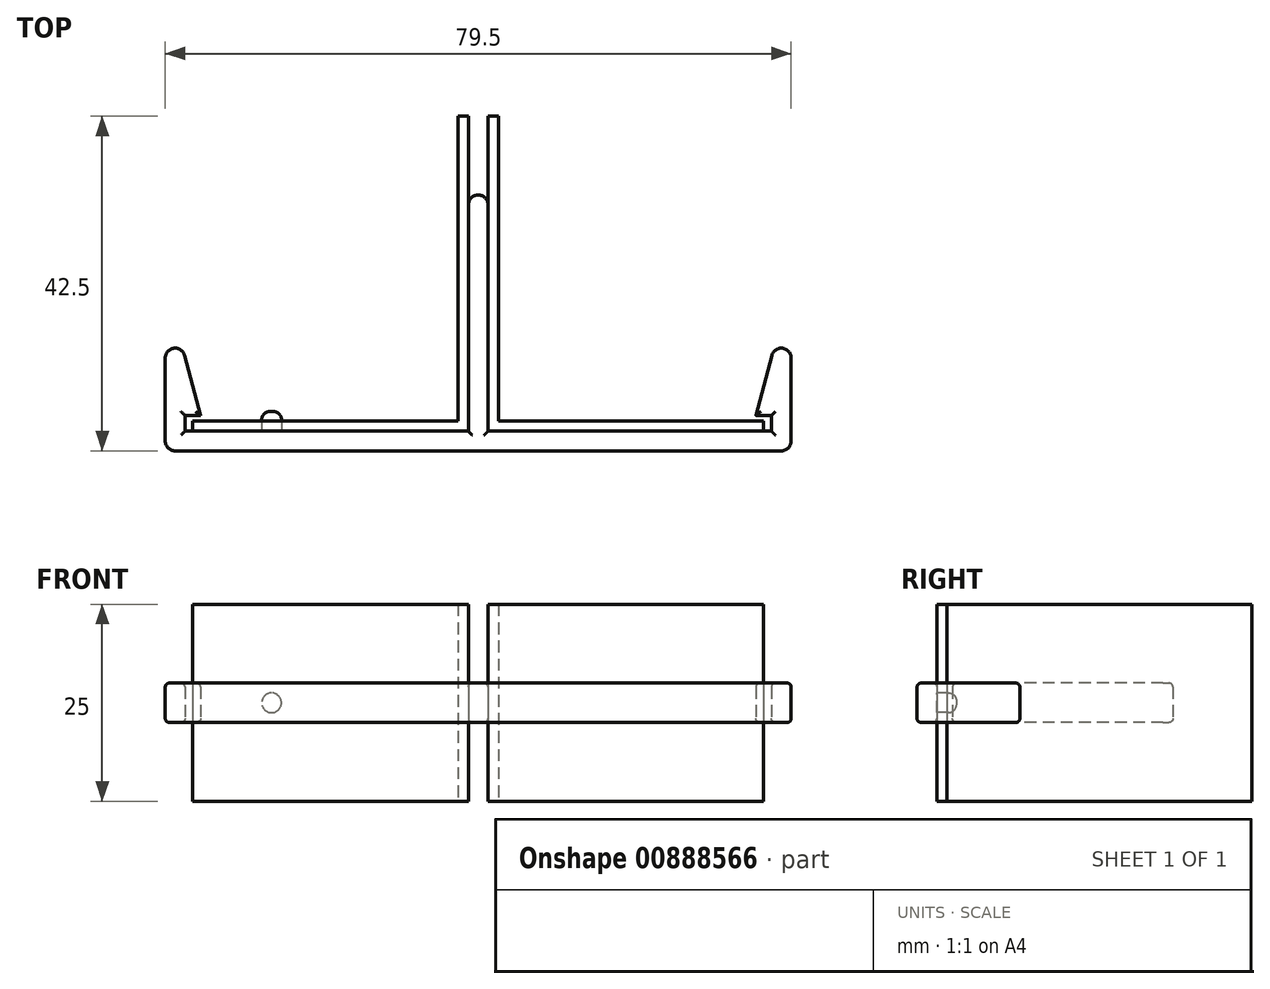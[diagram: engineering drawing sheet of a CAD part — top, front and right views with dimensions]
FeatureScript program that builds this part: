
annotation { "Feature Type Name" : "Feature", "Feature Type Description" : "" }
export const myFeature = defineFeature(function(context is Context, id is Id, definition is map)
    precondition{}
    {
        {
            var Q0;
            Q0=qCreatedBy(makeId("Top.planeOp"),FACE);
            var sketch = newSketch(context, id + "F0", { "sketchPlane" : qUnion([Q0])});
            skLineSegment(sketch, "E0", {"start": v(-1.25, 0) * mm, "end": v(-1.25, 40) * mm});
            skLineSegment(sketch, "E1", {"start": v(-1.25, 40) * mm, "end": v(-2.55, 40) * mm});
            skLineSegment(sketch, "E2", {"start": v(-2.55, 40) * mm, "end": v(-2.55, 1.3) * mm});
            skLineSegment(sketch, "E3", {"start": v(-2.55, 1.3) * mm, "end": v(-36.25, 1.3) * mm});
            skLineSegment(sketch, "E4", {"start": v(-36.25, 1.3) * mm, "end": v(-36.25, 0) * mm});
            skLineSegment(sketch, "E5", {"start": v(-36.25, 0) * mm, "end": v(-1.25, 0) * mm});
            skLineSegment(sketch, "E6.bottom", {"start": v(-28.25, 0) * mm, "end": v(-24.25, 0) * mm});
            skLineSegment(sketch, "E6.top", {"start": v(-28.25, 1.3) * mm, "end": v(-24.25, 1.3) * mm});
            skLineSegment(sketch, "E6.left", {"start": v(-28.25, 0) * mm, "end": v(-28.25, 1.3) * mm});
            skLineSegment(sketch, "E6.right", {"start": v(-24.25, 0) * mm, "end": v(-24.25, 1.3) * mm});
            skPoint(sketch, "E7", {"position": v(-26.25, 0) * mm});
            skSolve(sketch);
        }
        {
            var Q0;
            Q0=qCreatedBy(makeId("Top.planeOp"),FACE);
            var sketch = newSketch(context, id + "F1", { "sketchPlane" : qUnion([Q0])});
            skLineSegment(sketch, "E8", {"start": v(-37.25, 2) * mm, "end": v(-37.25, 0) * mm});
            skLineSegment(sketch, "E9", {"start": v(-37.25, 2) * mm, "end": v(-35.25, 2) * mm});
            skLineSegment(sketch, "E10", {"start": v(-35.25, 2) * mm, "end": v(-39.75, 18.8) * mm});
            skLineSegment(sketch, "E11", {"start": v(-39.75, 18.8) * mm, "end": v(-39.75, -2.5) * mm});
            skLineSegment(sketch, "E12", {"start": v(-39.75, -2.5) * mm, "end": v(0, -2.5) * mm});
            skLineSegment(sketch, "E13", {"start": v(0, -2.5) * mm, "end": v(0, 30) * mm});
            skLineSegment(sketch, "E14", {"start": v(0, 30) * mm, "end": v(-1.25, 30) * mm});
            skLineSegment(sketch, "E15", {"start": v(-1.25, 30) * mm, "end": v(-1.25, 0) * mm});
            skLineSegment(sketch, "E16", {"start": v(-1.25, 0) * mm, "end": v(-37.25, 0) * mm});
            skSolve(sketch);
        }
        {
            var Q0;
            Q0=makeQuery(id+"F1.imprint","IMPRINT",FACE,{"disambiguationData":[TD([[makeQuery(id+"F1.imprint","IMPRINT",EDGE,{"derivedFrom":sQuery(id+"F1.wireOp",EDGE,"E8")}),-1.0]])]});
            extrude(context, id + "F2", {"entities" : qUnion([Q0]), "endBound" : BoundingType.SYMMETRIC, "depth" : 5 * mm, "offsetDistance" : 25 * mm});
        }
        {
            var Q0;
            Q0=makeQuery(id+"F2.opExtrude","SWEPT_BODY",BODY,{"disambiguationData":[OSD([sQuery(id+"F1.wireOp",EDGE,"E8"),sQuery(id+"F1.wireOp",EDGE,"E9"),sQuery(id+"F1.wireOp",EDGE,"E10"),sQuery(id+"F1.wireOp",EDGE,"E11"),sQuery(id+"F1.wireOp",EDGE,"E12"),sQuery(id+"F1.wireOp",EDGE,"E13"),sQuery(id+"F1.wireOp",EDGE,"E14"),sQuery(id+"F1.wireOp",EDGE,"E15"),sQuery(id+"F1.wireOp",EDGE,"E16")])]});
            var Q1;
            Q1=qCreatedBy(makeId("Right.planeOp"),FACE);
            mirror(context, id + "F3", {"operationType" : NewBodyOperationType.ADD, "entities" : qUnion([Q0]), "mirrorPlane" : qUnion([Q1])});
        }
        {
            var Q0;
            Q0=makeQuery(id+"F2.opExtrude","SWEPT_FACE",FACE,{"disambiguationData":[OSD([sQuery(id+"F1.wireOp",EDGE,"E16")])]});
            var sketch = newSketch(context, id + "F4", { "sketchPlane" : qUnion([Q0])});
            skCircle(sketch, "E17", {"center": v(26.25, 0) * mm, "radius": 1.25 * mm});
            skSolve(sketch);
        }
        {
            var Q0;
            Q0=makeQuery(id+"F4.imprint","IMPRINT",FACE,{"disambiguationData":[TD([[makeQuery(id+"F4.imprint","IMPRINT",EDGE,{"derivedFrom":sQuery(id+"F4.wireOp",EDGE,"E17")}),1.0]])]});
            extrude(context, id + "F5", {"entities" : qUnion([Q0]), "operationType" : NewBodyOperationType.ADD, "depth" : 2.5 * mm, "offsetDistance" : 25 * mm});
        }
        {
            var Q0;
            Q0=makeQuery(id+"F5.opExtrude","CAP_FACE",FACE,{"disambiguationData":[OSD([sQuery(id+"F4.wireOp",EDGE,"E17")])],"isStart":false});
            fillet(context, id + "F6", {"entities" : qUnion([Q0]), "radius" : 1 * mm, "tangentPropagation" : true, "allowEdgeOverflow" : false});
        }
        {
            var Q0;
            {var subQ0=makeQuery(id+"F2.opExtrude","CAP_FACE",FACE,{"disambiguationData":[OSD([sQuery(id+"F1.wireOp",EDGE,"E8"),sQuery(id+"F1.wireOp",EDGE,"E9"),sQuery(id+"F1.wireOp",EDGE,"E10"),sQuery(id+"F1.wireOp",EDGE,"E11"),sQuery(id+"F1.wireOp",EDGE,"E12"),sQuery(id+"F1.wireOp",EDGE,"E13"),sQuery(id+"F1.wireOp",EDGE,"E14"),sQuery(id+"F1.wireOp",EDGE,"E15"),sQuery(id+"F1.wireOp",EDGE,"E16")])],"isStart":true});Q0=makeQuery(id+"F3.boolean.opBoolean","MERGE",FACE,{"derivedFrom":[subQ0,makeQuery(id+"F3.opPattern","COPY",FACE,{"derivedFrom":subQ0,"instanceName":"1"})]});}
            var Q1;
            {var subQ0=makeQuery(id+"F2.opExtrude","CAP_FACE",FACE,{"disambiguationData":[OSD([sQuery(id+"F1.wireOp",EDGE,"E8"),sQuery(id+"F1.wireOp",EDGE,"E9"),sQuery(id+"F1.wireOp",EDGE,"E10"),sQuery(id+"F1.wireOp",EDGE,"E11"),sQuery(id+"F1.wireOp",EDGE,"E12"),sQuery(id+"F1.wireOp",EDGE,"E13"),sQuery(id+"F1.wireOp",EDGE,"E14"),sQuery(id+"F1.wireOp",EDGE,"E15"),sQuery(id+"F1.wireOp",EDGE,"E16")])],"isStart":false});Q1=makeQuery(id+"F3.boolean.opBoolean","MERGE",FACE,{"derivedFrom":[subQ0,makeQuery(id+"F3.opPattern","COPY",FACE,{"derivedFrom":subQ0,"instanceName":"1"})]});}
            fillet(context, id + "F7", {"entities" : qUnion([Q0, Q1]), "radius" : 0.5 * mm, "tangentPropagation" : true, "allowEdgeOverflow" : false});
        }
        {
            var Q0;
            Q0=makeQuery(id+"F3.opPattern","COPY",EDGE,{"derivedFrom":makeQuery(id+"F2.opExtrude","SWEPT_EDGE",EDGE,{"disambiguationData":[OSD([sQuery(id+"F1.wireOp",EDGE,"E14"),sQuery(id+"F1.wireOp",EDGE,"E15")])]}),"instanceName":"1"});
            var Q1;
            Q1=makeQuery(id+"F2.opExtrude","SWEPT_EDGE",EDGE,{"disambiguationData":[OSD([sQuery(id+"F1.wireOp",EDGE,"E14"),sQuery(id+"F1.wireOp",EDGE,"E15")])]});
            var Q2;
            Q2=makeQuery(id+"F2.opExtrude","SWEPT_EDGE",EDGE,{"disambiguationData":[OSD([sQuery(id+"F1.wireOp",EDGE,"E10"),sQuery(id+"F1.wireOp",EDGE,"E11")])]});
            var Q3;
            Q3=makeQuery(id+"F3.opPattern","COPY",EDGE,{"derivedFrom":makeQuery(id+"F2.opExtrude","SWEPT_EDGE",EDGE,{"disambiguationData":[OSD([sQuery(id+"F1.wireOp",EDGE,"E10"),sQuery(id+"F1.wireOp",EDGE,"E11")])]}),"instanceName":"1"});
            var Q4;
            Q4=makeQuery(id+"F3.opPattern","COPY",EDGE,{"derivedFrom":makeQuery(id+"F2.opExtrude","SWEPT_EDGE",EDGE,{"disambiguationData":[OSD([sQuery(id+"F1.wireOp",EDGE,"E11"),sQuery(id+"F1.wireOp",EDGE,"E12")])]}),"instanceName":"1"});
            var Q5;
            Q5=makeQuery(id+"F2.opExtrude","SWEPT_EDGE",EDGE,{"disambiguationData":[OSD([sQuery(id+"F1.wireOp",EDGE,"E11"),sQuery(id+"F1.wireOp",EDGE,"E12")])]});
            fillet(context, id + "F8", {"entities" : qUnion([Q0, Q1, Q2, Q3, Q4, Q5]), "radius" : 1.25 * mm, "tangentPropagation" : true, "allowEdgeOverflow" : false});
        }
        {
            var Q0;
            {var subQ3=sQuery(id+"F0.wireOp",EDGE,"E0");Q0=makeQuery(id+"F0.imprint","IMPRINT",FACE,{"disambiguationData":[TD([[makeQuery(id+"F0.imprint","IMPRINT",EDGE,{"derivedFrom":subQ3}),1.0]])]});}
            var Q1;
            {var subQ2=sQuery(id+"F0.wireOp",EDGE,"E4");Q1=makeQuery(id+"F0.imprint","IMPRINT",FACE,{"disambiguationData":[TD([[makeQuery(id+"F0.imprint","IMPRINT",EDGE,{"derivedFrom":subQ2}),1.0]])]});}
            var Q2;
            {var subQ0=sQuery(id+"F0.wireOp",EDGE,"E6.left");Q2=makeQuery(id+"F0.imprint","IMPRINT",FACE,{"disambiguationData":[TD([[makeQuery(id+"F0.imprint","IMPRINT",EDGE,{"derivedFrom":subQ0}),-1.0]])]});}
            extrude(context, id + "F9", {"entities" : qUnion([Q0, Q1, Q2]), "endBound" : BoundingType.SYMMETRIC, "depth" : 25 * mm, "offsetDistance" : 25 * mm});
        }
        {
            var Q0;
            Q0=makeQuery(id+"F9.opExtrude","SWEPT_BODY",BODY,{"disambiguationData":[OSD([sQuery(id+"F0.wireOp",EDGE,"E0"),sQuery(id+"F0.wireOp",EDGE,"E1"),sQuery(id+"F0.wireOp",EDGE,"E2"),sQuery(id+"F0.wireOp",EDGE,"E3"),sQuery(id+"F0.wireOp",EDGE,"E4"),sQuery(id+"F0.wireOp",EDGE,"E5")])]});
            var Q1;
            Q1=qCreatedBy(makeId("Right.planeOp"),FACE);
            mirror(context, id + "F10", {"entities" : qUnion([Q0]), "mirrorPlane" : qUnion([Q1])});
        }
    });
